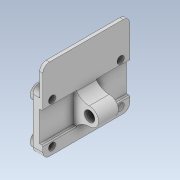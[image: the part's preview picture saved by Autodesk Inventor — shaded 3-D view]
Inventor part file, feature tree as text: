
AUTODESK INVENTOR PART (.ipt)
format: ipt  version: 2020.4 (Build 244396000, 396)  size: 241,152 bytes
history: native  units: mm
features: extrude x7, sketch x7, thread x5, fillet x2
ambient origin geometry x8: Origin, YZ Plane, XZ Plane, XY Plane, X Axis, Y Axis, Z Axis, Center Point
bodies: Solid1 (feature_tree)
feature tree (21):
  extrude  "Extrusion1"  Depth=25.0mm
  extrude  "Extrusion2"  Depth=2.2mm
  extrude  "Extrusion3"  Depth=3.0mm
  fillet  "Fillet1"  Radius=2.2mm
  thread  "Thread1"  [1 undecoded]
  thread  "Thread2"  [1 undecoded]
  thread  "Thread3"  [1 undecoded]
  thread  "Thread4"  [1 undecoded]
  extrude  "Extrusion4"  Depth=2.0mm
  extrude  "Extrusion5"  Depth=4.5mm TaperAngle=0.0deg
  fillet  "Fillet2"  Radius=4.5mm
  extrude  "Extrusion6"  Depth=1.0mm TaperAngle=0.0deg
  extrude  "Extrusion7"  Depth=10.0mm TaperAngle=0.0deg
  thread  "Thread5"  [1 undecoded]
  sketch  "Sketch3"  dims[d14=25.0mm d15=4.4mm]
  sketch  "Sketch5"  dims[d16=2.2mm d18=2.2mm]
  sketch  "Sketch6"  dims[d19=4.4mm d21=4.4mm d22=2.2mm d23=4.4mm d25=7.0mm d26=3.0mm d27=0.0mm]
  sketch  "Sketch7"  dims[d28=25.0mm d29=4.4mm d30=2.2mm d31=2.2mm d32=4.4mm d33=4.4mm d34=2.2mm d35=4.4mm d36=7.0mm d37=1.0mm d38=0.0mm]
  sketch  "Sketch8"  dims[d39=25.0mm d40=4.4mm d41=2.2mm d42=2.2mm d43=4.4mm d44=4.4mm d45=2.2mm d46=4.4mm d47=7.0mm d48=4.5mm d49=0.0mm d50=2.0mm]
  sketch  "Sketch9"  dims[d51=4.5mm d52=0.0mm d53=4.5mm d54=0.0mm d55=4.5mm d56=0.0mm]
  sketch  "Sketch10"  dims[d57=4.5mm d58=0.0mm d61=1.0mm d62=0.0mm d64=10.0mm d65=0.0mm d66=0.3mm d69=3.2mm d70=5.5mm d71=10.0mm d72=0.0mm d73=5.0mm d74=5.0mm d75=3.2mm d76=5.5mm d77=5.0mm d78=5.0mm d79=10.0mm d80=0.0mm d81=6.082mm d82=0.0mm]
note: 5 required parameter values undecoded (feature->parameter linkage not recoverable at this tier; creation-order binding heuristic only, values carry confidence <= 0.55)
